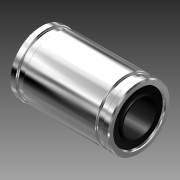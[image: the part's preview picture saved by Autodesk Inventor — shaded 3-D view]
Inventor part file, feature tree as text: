
AUTODESK INVENTOR PART (.ipt)
format: ipt  version: 2012 (Build 160160000, 160)  size: 184,832 bytes
history: native  units: in
note: dims shown in document units (in); Inventor stores cm internally (conversion verified against a paired STEP export)
features: chamfer x2, revolve x1, sketch x1
ambient origin geometry x8: Origin, YZ Plane, XZ Plane, XY Plane, X Axis, Y Axis, Z Axis, Center Point
bodies: Solid1 (feature_tree)
feature tree (4):
  revolve  "Revolution1"  [1 undecoded]
  chamfer  "Chamfer1"  Distance=0.2953in
  chamfer  "Chamfer2"  Distance=0.02in
  sketch  "Sketch1"  dims[d0=0.9252in d1=0.1575in d2=0.2953in d3=0.02in d4=0.9449in d5=0.9449in d6=0.063in d7=0.063in d8=90.0deg d9=0.01in d10=0.125in d11=45.0deg d12=0.005in d13=0.125in d14=45.0deg]
note: 1 required parameter value undecoded (feature->parameter linkage not recoverable at this tier; creation-order binding heuristic only, values carry confidence <= 0.55)
